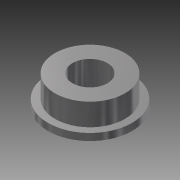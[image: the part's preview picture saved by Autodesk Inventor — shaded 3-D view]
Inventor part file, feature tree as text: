
AUTODESK INVENTOR PART (.ipt)
format: ipt  version: 2015 (Build 190159000, 159)  size: 110,592 bytes
history: native  units: mm
features: extrude x3, sketch x3, other x1
ambient origin geometry x8: Origin, YZ Plane, XZ Plane, XY Plane, X Axis, Y Axis, Z Axis, Center Point
bodies: Body1 (feature_tree)
feature tree (7):
  other  "ソリッド1"
  extrude  "押し出し1"  Depth=7.2mm
  extrude  "押し出し2"  Depth=0.6mm TaperAngle=0.0deg
  extrude  "押し出し3"  Depth=6.0mm
  sketch  "スケッチ1"
  sketch  "スケッチ2"
  sketch  "スケッチ3"
